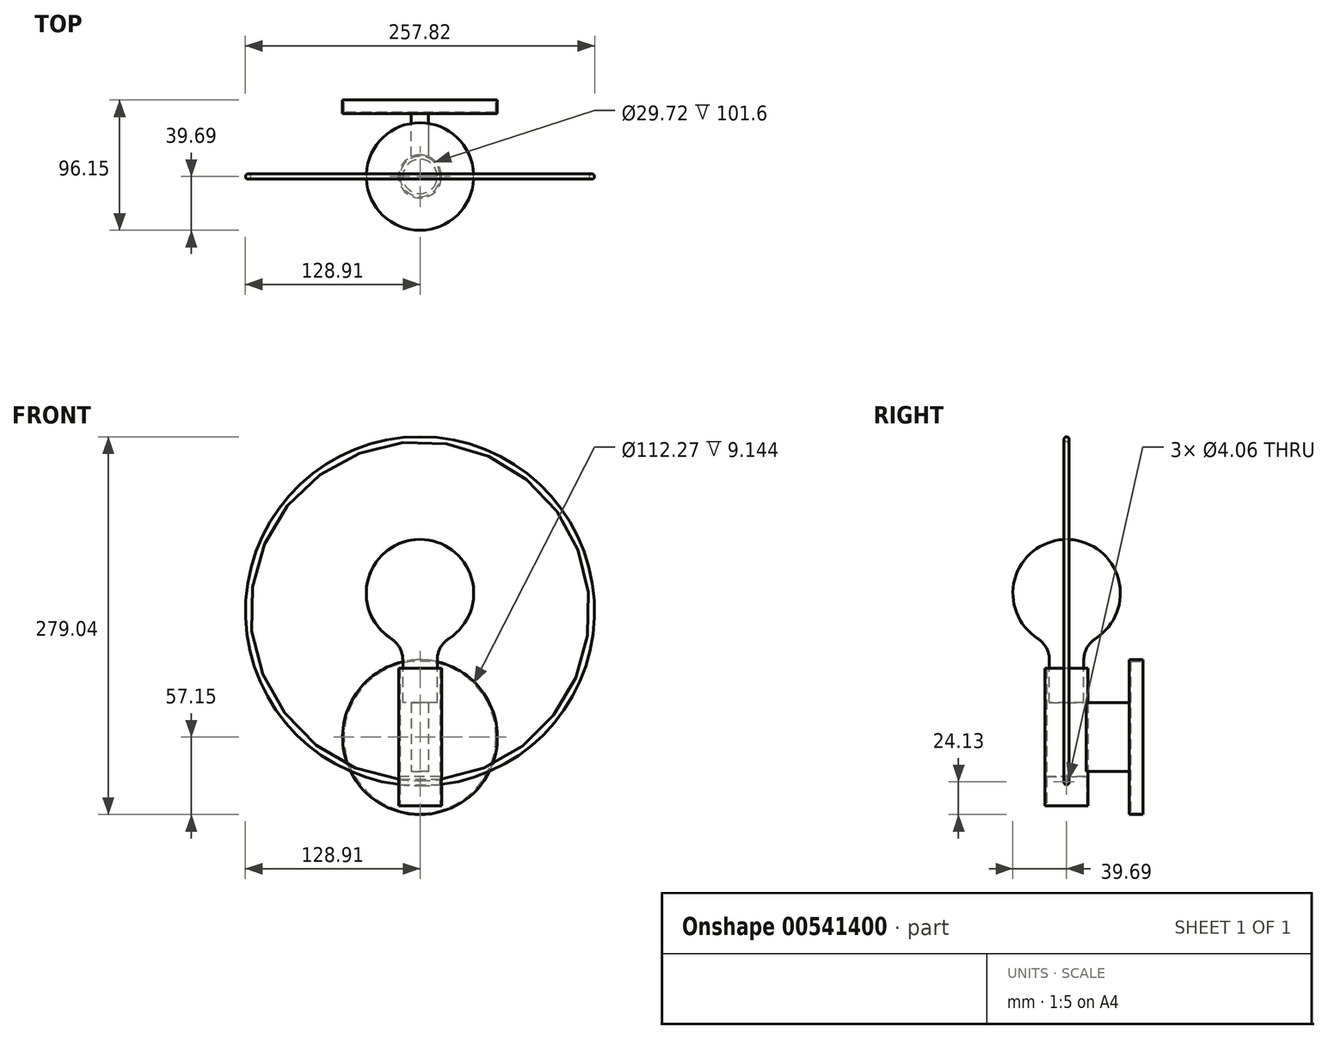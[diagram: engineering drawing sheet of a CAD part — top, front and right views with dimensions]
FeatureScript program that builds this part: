
annotation { "Feature Type Name" : "Feature", "Feature Type Description" : "" }
export const myFeature = defineFeature(function(context is Context, id is Id, definition is map)
    precondition{}
    {
        {
            var Q0;
            Q0=qCreatedBy(makeId("Top.planeOp"),FACE);
            var sketch = newSketch(context, id + "F0", { "sketchPlane" : qUnion([Q0])});
            skCircle(sketch, "E0", {"center": v(0, 0) * mm, "radius": 15.88 * mm});
            skCircle(sketch, "E1", {"center": v(0, 0) * mm, "radius": 14.86 * mm});
            skSolve(sketch);
        }
        {
            var Q0;
            Q0=makeQuery(id+"F0.imprint","IMPRINT",FACE,{"disambiguationData":[TD([[makeQuery(id+"F0.imprint","IMPRINT",EDGE,{"derivedFrom":sQuery(id+"F0.wireOp",EDGE,"E1")}),-1.0]])]});
            extrude(context, id + "F1", {"entities" : qUnion([Q0]), "depth" : 101.6 * mm, "offsetDistance" : 25.4 * mm});
        }
        {
            var Q0;
            Q0=makeQuery(id+"F0.imprint","IMPRINT",FACE,{"disambiguationData":[TD([[makeQuery(id+"F0.imprint","IMPRINT",EDGE,{"derivedFrom":sQuery(id+"F0.wireOp",EDGE,"E1")}),1.0]])]});
            var Q1;
            Q1=sQuery(id+"F0.wireOp",EDGE,"E1");
            extrude(context, id + "F2", {"entities" : qUnion([Q0]), "surfaceEntities" : qUnion([Q1]), "depth" : 21.59 * mm, "offsetDistance" : 25.4 * mm});
        }
        {
            var Q0;
            Q0=qCreatedBy(makeId("Front.planeOp"),FACE);
            var sketch = newSketch(context, id + "F3", { "sketchPlane" : qUnion([Q0])});
            skArc(sketch, "E2", {"start": v(21.45, 123.77) * mm, "mid": v(0, 196.85) * mm, "end": v(-21.45, 123.77) * mm});
            skLineSegment(sketch, "E3.top", {"start": v(-12.7, 76.2) * mm, "end": v(12.7, 76.2) * mm});
            skLineSegment(sketch, "E3.left", {"start": v(-12.7, 107.75) * mm, "end": v(-12.7, 76.2) * mm});
            skLineSegment(sketch, "E3.right", {"start": v(12.7, 107.75) * mm, "end": v(12.7, 76.2) * mm});
            skPoint(sketch, "E4.visualSharp", {"position": v(-12.7, 119.56) * mm});
            skArc(sketch, "E4.filletArc", {"start": v(-12.7, 107.75) * mm, "mid": v(-15.03, 116.88) * mm, "end": v(-21.45, 123.77) * mm});
            skPoint(sketch, "E5.visualSharp", {"position": v(12.7, 119.56) * mm});
            skArc(sketch, "E5.filletArc", {"start": v(21.45, 123.77) * mm, "mid": v(15.03, 116.88) * mm, "end": v(12.7, 107.75) * mm});
            skLineSegment(sketch, "E6", {"start": v(0, 196.85) * mm, "end": v(0, 76.2) * mm});
            skSolve(sketch);
        }
        {
            var Q0;
            {var subQ0=sQuery(id+"F3.wireOp",EDGE,"E3.left");Q0=makeQuery(id+"F3.imprint","IMPRINT",FACE,{"disambiguationData":[TD([[makeQuery(id+"F3.imprint","IMPRINT",EDGE,{"derivedFrom":subQ0}),1.0]])]});}
            var Q1;
            Q1=sQuery(id+"F3.wireOp",EDGE,"E6");
            revolve(context, id + "F4", {"entities" : qUnion([Q0]), "axis" : qUnion([Q1]), "revolveType" : RevolveType.FULL});
        }
        {
            var Q0;
            Q0=qCreatedBy(makeId("Right.planeOp"),FACE);
            var sketch = newSketch(context, id + "F5", { "sketchPlane" : qUnion([Q0])});
            skCircle(sketch, "E7", {"center": v(0, 17.78) * mm, "radius": 2.03 * mm});
            skSolve(sketch);
        }
        {
            var Q0;
            Q0 = qSketchRegion(id + "F5", true);
            extrude(context, id + "F6", {"entities" : qUnion([Q0]), "operationType" : NewBodyOperationType.REMOVE, "endBound" : BoundingType.THROUGH_ALL, "oppositeDirection" : true, "depth" : 25.4 * mm, "offsetDistance" : 25.4 * mm, "hasSecondDirection" : true, "secondDirectionBound" : BoundingType.THROUGH_ALL, "secondDirectionOppositeDirection" : false, "secondDirectionDepth" : 25.4 * mm});
        }
        {
            var Q0;
            Q0=qCreatedBy(makeId("Front.planeOp"),FACE);
            var sketch = newSketch(context, id + "F7", { "sketchPlane" : qUnion([Q0])});
            skCircle(sketch, "E8", {"center": v(0, 143.78) * mm, "radius": 127 * mm});
            skFitSpline(sketch, "E9.0", {"points": [v(-15.88, 19.81) * mm, v(-15.88, 19.81) * mm, v(-15.86, 19.7) * mm, v(-15.8, 19.25) * mm, v(-15.77, 18.7) * mm, v(-15.75, 18.18) * mm, v(-15.74, 17.78) * mm, v(-15.75, 17.38) * mm, v(-15.76, 17) * mm, v(-15.78, 16.64) * mm, v(-15.82, 16.23) * mm, v(-15.86, 15.85) * mm, v(-15.88, 15.75) * mm, v(-15.87, 15.75) * mm], "construction": true});
            skLineSegment(sketch, "E10", {"start": v(-15.88, 19.81) * mm, "end": v(-15.87, 15.75) * mm, "construction": true});
            skPoint(sketch, "E11", {"position": v(-15.87, 17.78) * mm});
            skSolve(sketch);
        }
        {
            var Q0;
            Q0=qCreatedBy(makeId("Right.planeOp"),FACE);
            var sketch = newSketch(context, id + "F8", { "sketchPlane" : qUnion([Q0])});
            skCircle(sketch, "E12", {"center": v(0, 16.78) * mm, "radius": 1.9 * mm});
            skSolve(sketch);
        }
        {
            var Q0;
            Q0 = qSketchRegion(id + "F8", true);
            var Q1;
            Q1 = qConstructionFilter(qBodyType(qCreatedBy(id + "F7" ,EDGE), BodyType.WIRE), ConstructionObject.NO);
            sweep(context, id + "F9", {"profiles" : qUnion([Q0]), "path" : qUnion([Q1])});
        }
        {
            var Q0;
            Q0=makeQuery(id+"F1.opExtrude","CAP_FACE",FACE,{"disambiguationData":[OSD([sQuery(id+"F0.wireOp",EDGE,"E0"),sQuery(id+"F0.wireOp",EDGE,"E1")])],"isStart":false});
            var Q1;
            Q1=makeQuery(id+"F0.imprint","IMPRINT",FACE,{"disambiguationData":[TD([[makeQuery(id+"F0.imprint","IMPRINT",EDGE,{"derivedFrom":sQuery(id+"F0.wireOp",EDGE,"E0")}),1.0]])]});
            cPlane(context, id + "F10", {"entities" : qUnion([Q0, Q1]), "cplaneType" : CPlaneType.MID_PLANE, "offset" : 25.4 * mm, "width" : 152.4 * mm, "height" : 152.4 * mm});
        }
        {
            var Q0;
            Q0=qCreatedBy(id+"F10.planeOp",FACE);
            var sketch = newSketch(context, id + "F11", { "sketchPlane" : qUnion([Q0])});
            skCircle(sketch, "E13", {"center": v(0, 0) * mm, "radius": 15.88 * mm});
            skLineSegment(sketch, "E14", {"start": v(-6.35, 14.55) * mm, "end": v(-6.35, 46.3) * mm});
            skLineSegment(sketch, "E15", {"start": v(-6.35, 46.3) * mm, "end": v(6.35, 46.3) * mm});
            skLineSegment(sketch, "E16", {"start": v(6.35, 46.3) * mm, "end": v(6.35, 14.55) * mm});
            skSolve(sketch);
        }
        {
            var Q0;
            {var subQ0=sQuery(id+"F11.wireOp",EDGE,"E14");Q0=makeQuery(id+"F11.imprint","IMPRINT",FACE,{"disambiguationData":[TD([[makeQuery(id+"F11.imprint","IMPRINT",EDGE,{"derivedFrom":subQ0}),-1.0]])]});}
            var Q1;
            Q1=makeQuery(id+"F1.opExtrude","CAP_FACE",FACE,{"disambiguationData":[OSD([sQuery(id+"F0.wireOp",EDGE,"E0"),sQuery(id+"F0.wireOp",EDGE,"E1")])],"isStart":false});
            var Q2;
            Q2=makeQuery(id+"F1.opExtrude","CAP_FACE",FACE,{"disambiguationData":[OSD([sQuery(id+"F0.wireOp",EDGE,"E0"),sQuery(id+"F0.wireOp",EDGE,"E1")])],"isStart":true});
            extrude(context, id + "F12", {"entities" : qUnion([Q0]), "depth" : 25.4 * mm, "endBoundEntityFace" : qUnion([Q1]), "offsetDistance" : 25.4 * mm, "hasSecondDirection" : true, "secondDirectionOppositeDirection" : true, "secondDirectionDepth" : 25.4 * mm, "secondDirectionBoundEntityFace" : qUnion([Q2])});
        }
        {
            var Q0;
            Q0=qCreatedBy(id+"F10.planeOp",FACE);
            var sketch = newSketch(context, id + "F13", { "sketchPlane" : qUnion([Q0])});
            skLineSegment(sketch, "E17", {"start": v(0, 46.3) * mm, "end": v(-57.15, 46.3) * mm});
            skLineSegment(sketch, "E18", {"start": v(-57.15, 46.3) * mm, "end": v(-57.15, 56.46) * mm});
            skLineSegment(sketch, "E19", {"start": v(-57.15, 56.46) * mm, "end": v(-56.13, 56.46) * mm});
            skLineSegment(sketch, "E20", {"start": v(-56.13, 56.46) * mm, "end": v(-56.13, 47.32) * mm});
            skLineSegment(sketch, "E21", {"start": v(-56.13, 47.32) * mm, "end": v(0, 47.32) * mm});
            skLineSegment(sketch, "E22", {"start": v(0, 47.32) * mm, "end": v(0, 46.3) * mm});
            skSolve(sketch);
        }
        {
            var Q0;
            Q0 = qSketchRegion(id + "F13", true);
            var Q1;
            Q1=sQuery(id+"F13.wireOp",EDGE,"E22");
            revolve(context, id + "F14", {"entities" : qUnion([Q0]), "axis" : qUnion([Q1]), "revolveType" : RevolveType.FULL});
        }
    });
